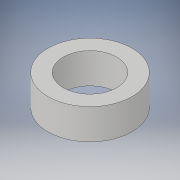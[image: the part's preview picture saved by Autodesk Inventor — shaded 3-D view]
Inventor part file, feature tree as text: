
AUTODESK INVENTOR PART (.ipt)
format: ipt  version: 2018 (Build 220112000, 112)  size: 96,768 bytes
history: native  units: in
note: dims shown in document units (in); Inventor stores cm internally (conversion verified against a paired STEP export)
features: extrude x1, sketch x1
ambient origin geometry x8: Origin, YZ Plane, XZ Plane, XY Plane, X Axis, Y Axis, Z Axis, Center Point
bodies: Solid1 (feature_tree)
feature tree (2):
  extrude  "Extrusion1"  Depth=0.0787in
  sketch  "Sketch1"  dims[d0=0.1378in d1=0.2165in d2=0.0787in d3=0.0in]
